SOLIDWORKS PART (.sldprt)
format: sldprt  version: not decoded by parser v0  size: 144,896 bytes
history: native  units: mm
features: plane x3, sketch x3, extrude x2, material x1, cut_revolve x1, chamfer x1 (+8 scaffold rows collapsed)
feature tree (19):
  scaffold x8  (default folders/planes/origin — collapsed)
  material  "Matériau <non spécifié>"
  plane  "Face"
  plane  "Dessus"
  plane  "Droite"
  sketch  "Esquisse1"  dims[D1=8.0mm]
  extrude  "Extrusion1"  Depth=12.5mm
  sketch  "Esquisse3"  dims[c1.D1=8.0mm c1.D6=0.5mm c1.D7=1.5mm c1.D2=4.0mm c1.D3=4.0mm c2.D3=30.0deg c2.D4=9.0mm c2.D5=3.5mm]
  cut_revolve  "Enlèvement de matière-Révolution1"  Angle=360deg
  sketch  "Esquisse4"  dims[D1=5.0mm]
  extrude  "Extrusion2"  Depth=12mm
  chamfer  "Chanfrein1"  Distance=0.5mm Angle=45deg
decode coverage: 7 of 7 modeling features carry decoded parameters
note: suppression state not decoded; provenance and decode notes live in map.json
